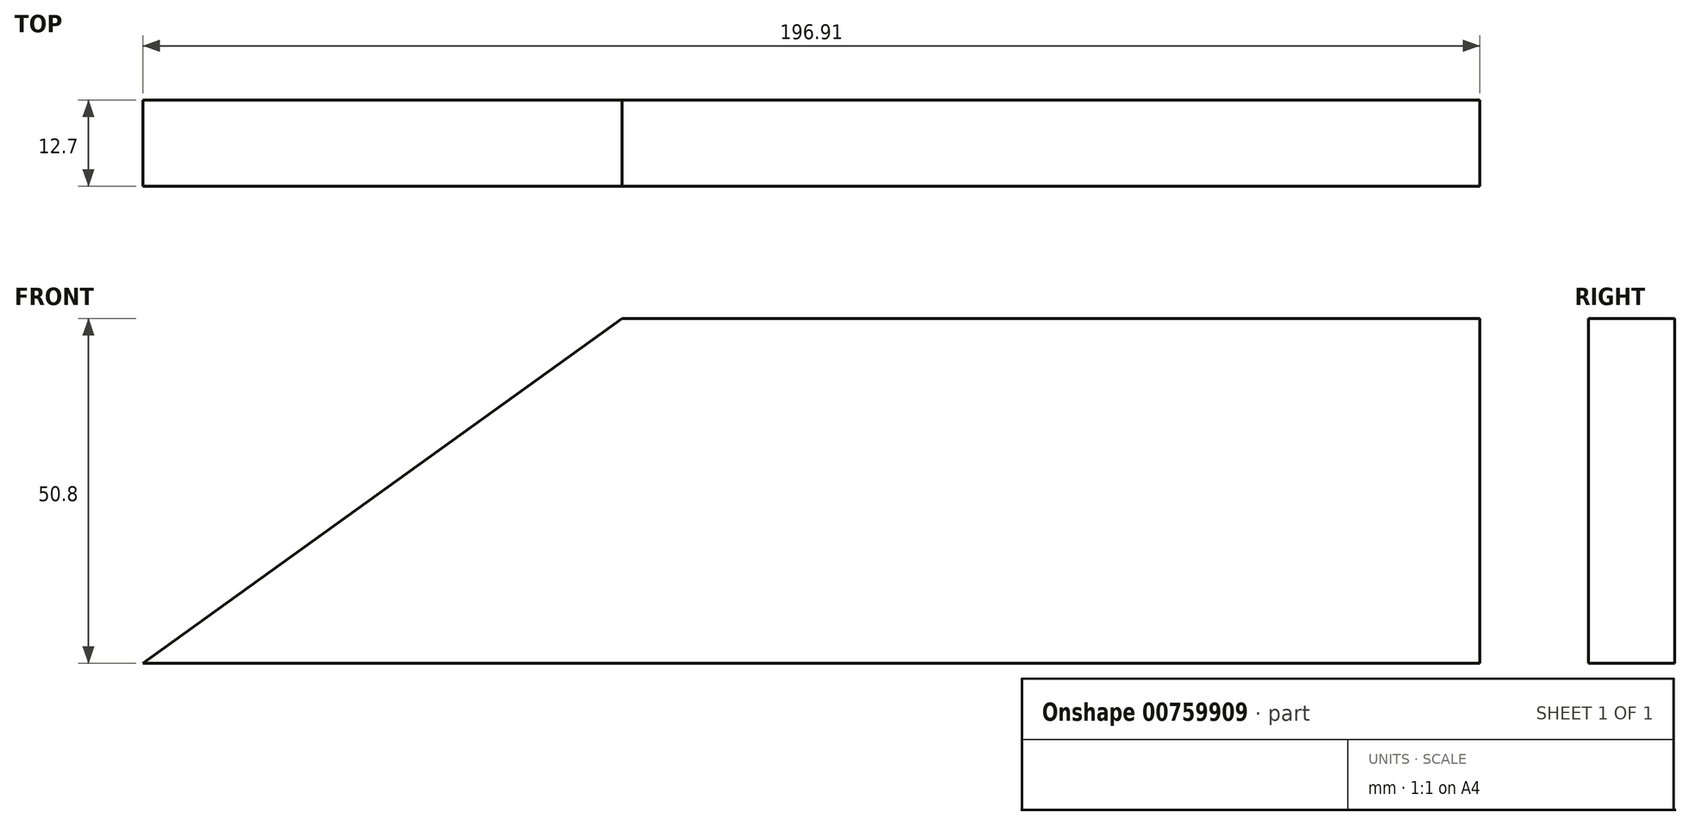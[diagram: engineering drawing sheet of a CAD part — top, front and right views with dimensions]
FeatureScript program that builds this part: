
annotation { "Feature Type Name" : "Feature", "Feature Type Description" : "" }
export const myFeature = defineFeature(function(context is Context, id is Id, definition is map)
    precondition{}
    {
        {
            var Q0;
            Q0=qCreatedBy(makeId("Front.planeOp"),FACE);
            var sketch = newSketch(context, id + "F0", { "sketchPlane" : qUnion([Q0])});
            skLineSegment(sketch, "E0.bottom", {"start": v(-29.9, 23.03) * mm, "end": v(96.46, 23.03) * mm});
            skLineSegment(sketch, "E0.top", {"start": v(-29.9, -27.77) * mm, "end": v(96.46, -27.77) * mm});
            skLineSegment(sketch, "E0.left", {"start": v(-29.9, 23.03) * mm, "end": v(-29.9, -27.77) * mm});
            skLineSegment(sketch, "E0.right", {"start": v(96.46, 23.03) * mm, "end": v(96.46, -27.77) * mm});
            skLineSegment(sketch, "E1", {"start": v(-29.9, -27.77) * mm, "end": v(-100.45, -27.77) * mm});
            skLineSegment(sketch, "E2", {"start": v(-29.9, 23.03) * mm, "end": v(-100.45, -27.77) * mm});
            skSolve(sketch);
        }
        {
            var Q0;
            Q0=makeQuery(id+"F0.imprint","IMPRINT",FACE,{"disambiguationData":[TD([[makeQuery(id+"F0.imprint","IMPRINT",EDGE,{"derivedFrom":sQuery(id+"F0.wireOp",EDGE,"E0.left")}),-1.0]])]});
            var Q1;
            Q1=makeQuery(id+"F0.imprint","IMPRINT",FACE,{"disambiguationData":[TD([[makeQuery(id+"F0.imprint","IMPRINT",EDGE,{"derivedFrom":sQuery(id+"F0.wireOp",EDGE,"E0.bottom")}),-1.0]])]});
            extrude(context, id + "F1", {"entities" : qUnion([Q0, Q1]), "depth" : 12.7 * mm, "offsetDistance" : 25.4 * mm});
        }
    });
